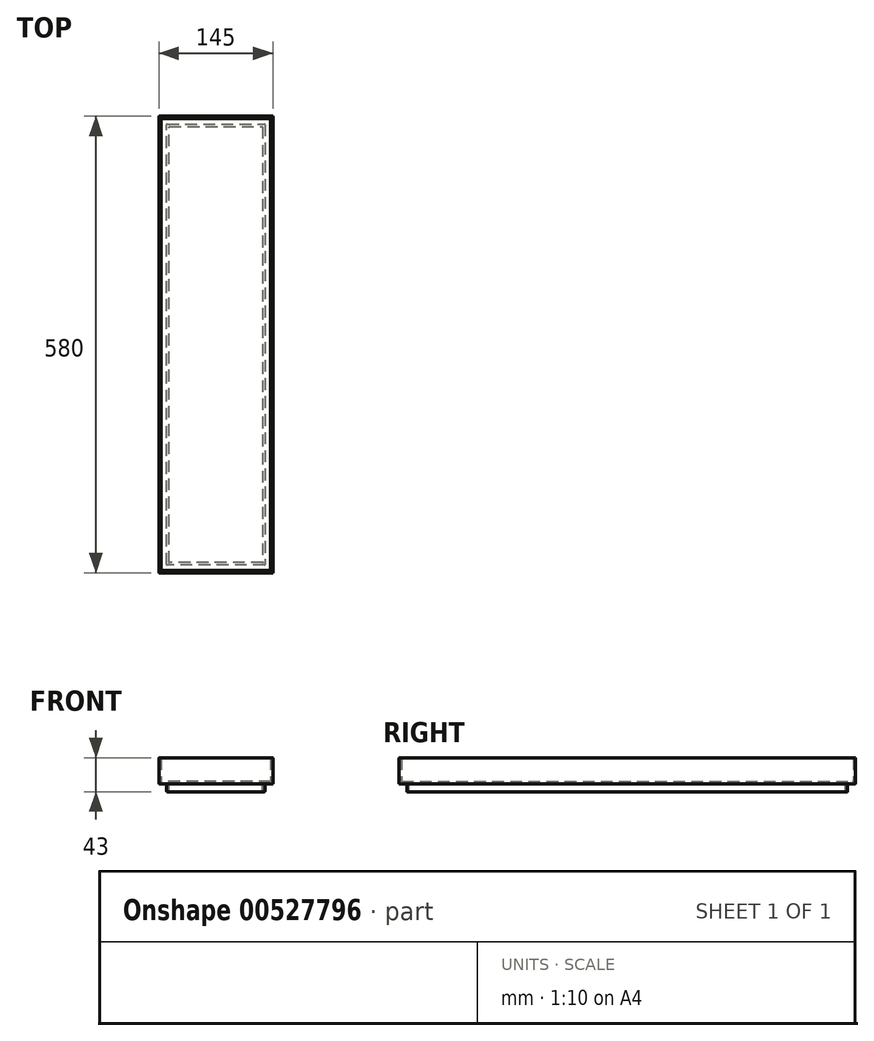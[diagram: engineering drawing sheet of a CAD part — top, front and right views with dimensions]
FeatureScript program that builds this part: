
annotation { "Feature Type Name" : "Feature", "Feature Type Description" : "" }
export const myFeature = defineFeature(function(context is Context, id is Id, definition is map)
    precondition{}
    {
        {
            var Q0;
            Q0=qCreatedBy(makeId("Top.planeOp"),FACE);
            var sketch = newSketch(context, id + "F0", { "sketchPlane" : qUnion([Q0])});
            skLineSegment(sketch, "E0.bottom", {"start": v(-72.5, 290) * mm, "end": v(72.5, 290) * mm});
            skLineSegment(sketch, "E0.top", {"start": v(-72.5, -290) * mm, "end": v(72.5, -290) * mm});
            skLineSegment(sketch, "E0.left", {"start": v(-72.5, 290) * mm, "end": v(-72.5, -290) * mm});
            skLineSegment(sketch, "E0.right", {"start": v(72.5, 290) * mm, "end": v(72.5, -290) * mm});
            skPoint(sketch, "E0.middle", {"position": v(0, 0) * mm});
            skSolve(sketch);
        }
        {
            var Q0;
            Q0 = qSketchRegion(id + "F0", true);
            extrude(context, id + "F1", {"entities" : qUnion([Q0]), "depth" : 3 * mm, "offsetDistance" : 25 * mm});
        }
        {
            var Q0;
            Q0=makeQuery(id+"F1.opExtrude","CAP_FACE",FACE,{"disambiguationData":[OSD([sQuery(id+"F0.wireOp",EDGE,"E0.bottom"),sQuery(id+"F0.wireOp",EDGE,"E0.top"),sQuery(id+"F0.wireOp",EDGE,"E0.left"),sQuery(id+"F0.wireOp",EDGE,"E0.right")])],"isStart":false});
            var sketch = newSketch(context, id + "F2", { "sketchPlane" : qUnion([Q0])});
            skLineSegment(sketch, "E1.0.0", {"start": v(-72.5, 290) * mm, "end": v(-72.5, -290) * mm});
            skLineSegment(sketch, "E1.0.1", {"start": v(-72.5, -290) * mm, "end": v(72.5, -290) * mm});
            skLineSegment(sketch, "E1.0.2", {"start": v(72.5, -290) * mm, "end": v(72.5, 290) * mm});
            skLineSegment(sketch, "E1.0.3", {"start": v(72.5, 290) * mm, "end": v(-72.5, 290) * mm});
            skLineSegment(sketch, "E2.0", {"start": v(-69.5, 287) * mm, "end": v(-69.5, -287) * mm});
            skLineSegment(sketch, "E2.1", {"start": v(69.5, 287) * mm, "end": v(-69.5, 287) * mm});
            skLineSegment(sketch, "E2.2", {"start": v(69.5, -287) * mm, "end": v(69.5, 287) * mm});
            skLineSegment(sketch, "E2.3", {"start": v(-69.5, -287) * mm, "end": v(69.5, -287) * mm});
            skSolve(sketch);
        }
        {
            var Q0;
            Q0 = qSketchRegion(id + "F2", true);
            extrude(context, id + "F3", {"entities" : qUnion([Q0]), "operationType" : NewBodyOperationType.ADD, "depth" : 30 * mm, "offsetDistance" : 25 * mm});
        }
        {
            var Q0;
            Q0=makeQuery(id+"F1.opExtrude","CAP_FACE",FACE,{"disambiguationData":[OSD([sQuery(id+"F0.wireOp",EDGE,"E0.bottom"),sQuery(id+"F0.wireOp",EDGE,"E0.top"),sQuery(id+"F0.wireOp",EDGE,"E0.left"),sQuery(id+"F0.wireOp",EDGE,"E0.right")])],"isStart":true});
            var sketch = newSketch(context, id + "F4", { "sketchPlane" : qUnion([Q0])});
            skLineSegment(sketch, "E3.0.0", {"start": v(-72.5, 290) * mm, "end": v(-72.5, -290) * mm, "construction": true});
            skLineSegment(sketch, "E3.0.1", {"start": v(-72.5, -290) * mm, "end": v(72.5, -290) * mm, "construction": true});
            skLineSegment(sketch, "E3.0.2", {"start": v(72.5, -290) * mm, "end": v(72.5, 290) * mm, "construction": true});
            skLineSegment(sketch, "E3.0.3", {"start": v(72.5, 290) * mm, "end": v(-72.5, 290) * mm, "construction": true});
            skLineSegment(sketch, "E4.0", {"start": v(-62.5, 280) * mm, "end": v(-62.5, -280) * mm});
            skLineSegment(sketch, "E4.1", {"start": v(62.5, 280) * mm, "end": v(-62.5, 280) * mm});
            skLineSegment(sketch, "E4.2", {"start": v(62.5, -280) * mm, "end": v(62.5, 280) * mm});
            skLineSegment(sketch, "E4.3", {"start": v(-62.5, -280) * mm, "end": v(62.5, -280) * mm});
            skLineSegment(sketch, "E5.0", {"start": v(-59.5, -277) * mm, "end": v(59.5, -277) * mm});
            skLineSegment(sketch, "E5.1", {"start": v(-59.5, 277) * mm, "end": v(-59.5, -277) * mm});
            skLineSegment(sketch, "E5.2", {"start": v(59.5, 277) * mm, "end": v(-59.5, 277) * mm});
            skLineSegment(sketch, "E5.3", {"start": v(59.5, -277) * mm, "end": v(59.5, 277) * mm});
            skSolve(sketch);
        }
        {
            var Q0;
            Q0 = qSketchRegion(id + "F4", true);
            extrude(context, id + "F5", {"entities" : qUnion([Q0]), "operationType" : NewBodyOperationType.ADD, "depth" : 10 * mm, "offsetDistance" : 25 * mm});
        }
        {
            var Q0;
            {var subQ0=sQuery(id+"F0.wireOp",EDGE,"E0.left");var subQ1=sQuery(id+"F0.wireOp",EDGE,"E0.bottom");var subQ2=sQuery(id+"F0.wireOp",EDGE,"E0.right");var subQ3=sQuery(id+"F0.wireOp",EDGE,"E0.top");Q0=makeQuery(id+"F5.boolean.opBoolean","SPLIT",FACE,{"disambiguationData":[TD([makeQuery(id+"F1.opExtrude","SWEPT_FACE",FACE,{"disambiguationData":[OSD([subQ1])]})])],"derivedFrom":makeQuery(id+"F1.opExtrude","CAP_FACE",FACE,{"disambiguationData":[OSD([subQ1,subQ3,subQ0,subQ2])],"isStart":true})});}
            var Q1;
            Q1=makeQuery(id+"F5.boolean.opBoolean","SPLIT",FACE,{"disambiguationData":[TD([makeQuery(id+"F5.opExtrude","SWEPT_FACE",FACE,{"disambiguationData":[OSD([sQuery(id+"F4.wireOp",EDGE,"E5.0")])]})])],"derivedFrom":makeQuery(id+"F1.opExtrude","CAP_FACE",FACE,{"disambiguationData":[OSD([sQuery(id+"F0.wireOp",EDGE,"E0.bottom"),sQuery(id+"F0.wireOp",EDGE,"E0.top"),sQuery(id+"F0.wireOp",EDGE,"E0.left"),sQuery(id+"F0.wireOp",EDGE,"E0.right")])],"isStart":true})});
            var Q2;
            Q2=makeQuery(id+"F5.opExtrude","SWEPT_EDGE",EDGE,{"disambiguationData":[OSD([sQuery(id+"F4.wireOp",EDGE,"E4.0"),sQuery(id+"F4.wireOp",EDGE,"E4.3")])]});
            var Q3;
            Q3=makeQuery(id+"F5.opExtrude","CAP_FACE",FACE,{"disambiguationData":[OSD([sQuery(id+"F4.wireOp",EDGE,"E4.0"),sQuery(id+"F4.wireOp",EDGE,"E4.1"),sQuery(id+"F4.wireOp",EDGE,"E4.2"),sQuery(id+"F4.wireOp",EDGE,"E4.3"),sQuery(id+"F4.wireOp",EDGE,"E5.0"),sQuery(id+"F4.wireOp",EDGE,"E5.1"),sQuery(id+"F4.wireOp",EDGE,"E5.2"),sQuery(id+"F4.wireOp",EDGE,"E5.3")])],"isStart":false});
            var Q4;
            Q4=makeQuery(id+"F5.opExtrude","SWEPT_FACE",FACE,{"disambiguationData":[OSD([sQuery(id+"F4.wireOp",EDGE,"E5.0")])]});
            var Q5;
            Q5=makeQuery(id+"F5.opExtrude","SWEPT_FACE",FACE,{"disambiguationData":[OSD([sQuery(id+"F4.wireOp",EDGE,"E4.1")])]});
            var Q6;
            Q6=makeQuery(id+"F5.opExtrude","SWEPT_FACE",FACE,{"disambiguationData":[OSD([sQuery(id+"F4.wireOp",EDGE,"E4.2")])]});
            var Q7;
            Q7=makeQuery(id+"F3.boolean.opBoolean","MERGE",FACE,{"derivedFrom":[makeQuery(id+"F1.opExtrude","SWEPT_FACE",FACE,{"disambiguationData":[OSD([sQuery(id+"F0.wireOp",EDGE,"E0.top")])]}),makeQuery(id+"F3.opExtrude","SWEPT_FACE",FACE,{"disambiguationData":[OSD([sQuery(id+"F2.wireOp",EDGE,"E1.0.1")])]})]});
            var Q8;
            Q8=makeQuery(id+"F3.boolean.opBoolean","MERGE",FACE,{"derivedFrom":[makeQuery(id+"F1.opExtrude","SWEPT_FACE",FACE,{"disambiguationData":[OSD([sQuery(id+"F0.wireOp",EDGE,"E0.right")])]}),makeQuery(id+"F3.opExtrude","SWEPT_FACE",FACE,{"disambiguationData":[OSD([sQuery(id+"F2.wireOp",EDGE,"E1.0.2")])]})]});
            var Q9;
            Q9=makeQuery(id+"F3.boolean.opBoolean","MERGE",FACE,{"derivedFrom":[makeQuery(id+"F1.opExtrude","SWEPT_FACE",FACE,{"disambiguationData":[OSD([sQuery(id+"F0.wireOp",EDGE,"E0.bottom")])]}),makeQuery(id+"F3.opExtrude","SWEPT_FACE",FACE,{"disambiguationData":[OSD([sQuery(id+"F2.wireOp",EDGE,"E1.0.3")])]})]});
            var Q10;
            Q10=makeQuery(id+"F3.opExtrude","CAP_EDGE",EDGE,{"disambiguationData":[OSD([sQuery(id+"F2.wireOp",EDGE,"E2.2")])],"isStart":false});
            var Q11;
            Q11=makeQuery(id+"F3.opExtrude","CAP_EDGE",EDGE,{"disambiguationData":[OSD([sQuery(id+"F2.wireOp",EDGE,"E2.1")])],"isStart":true});
            var Q12;
            Q12=makeQuery(id+"F3.opExtrude","SWEPT_FACE",FACE,{"disambiguationData":[OSD([sQuery(id+"F2.wireOp",EDGE,"E2.0")])]});
            var Q13;
            Q13=makeQuery(id+"F3.opExtrude","SWEPT_FACE",FACE,{"disambiguationData":[OSD([sQuery(id+"F2.wireOp",EDGE,"E2.3")])]});
            var Q14;
            Q14=makeQuery(id+"F3.opExtrude","CAP_EDGE",EDGE,{"disambiguationData":[OSD([sQuery(id+"F2.wireOp",EDGE,"E1.0.3")])],"isStart":false});
            var Q15;
            Q15=makeQuery(id+"F3.opExtrude","CAP_EDGE",EDGE,{"disambiguationData":[OSD([sQuery(id+"F2.wireOp",EDGE,"E1.0.0")])],"isStart":false});
            fillet(context, id + "F6", {"entities" : qUnion([Q0, Q1, Q2, Q3, Q4, Q5, Q6, Q7, Q8, Q9, Q10, Q11, Q12, Q13, Q14, Q15]), "radius" : 0.5 * mm, "tangentPropagation" : true, "allowEdgeOverflow" : false});
        }
    });
